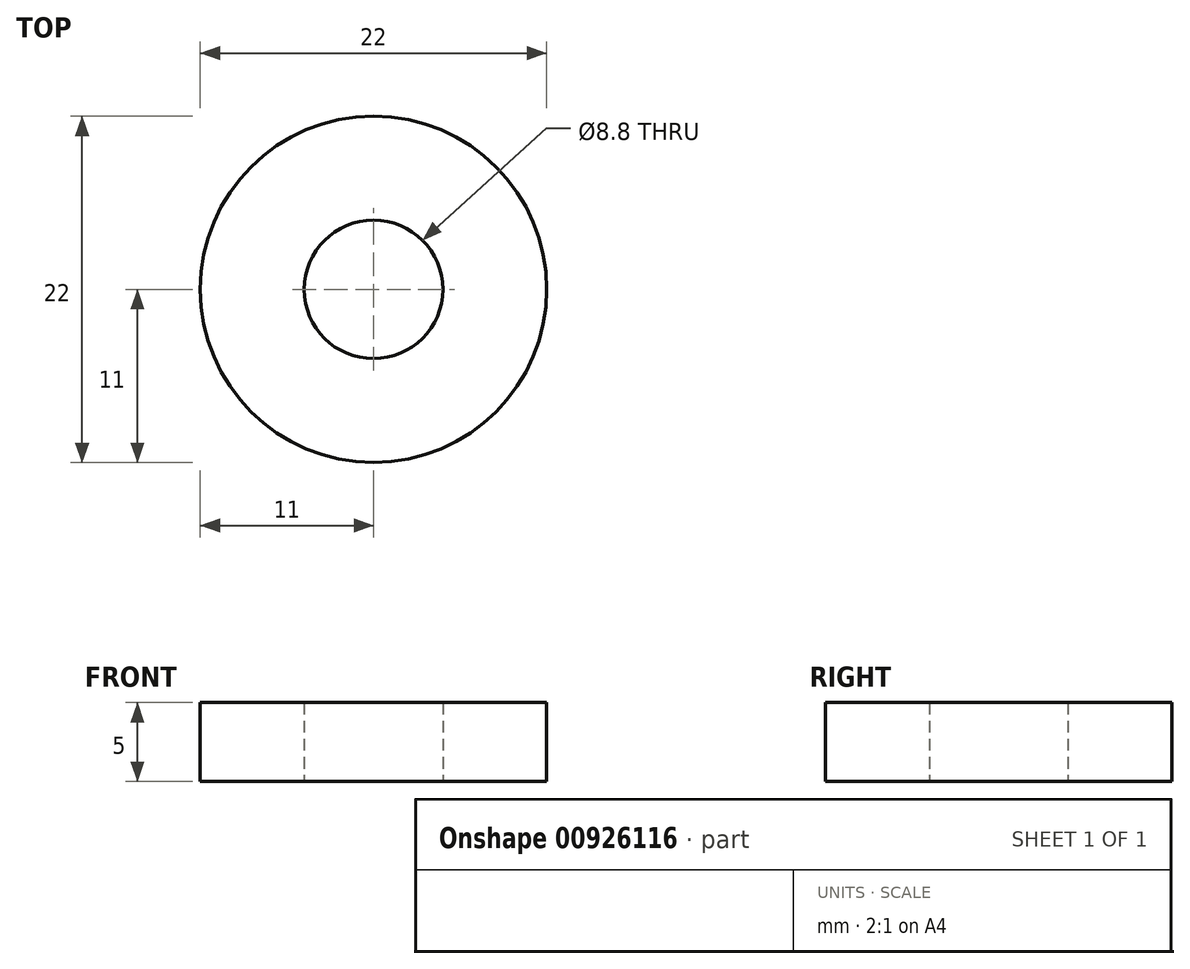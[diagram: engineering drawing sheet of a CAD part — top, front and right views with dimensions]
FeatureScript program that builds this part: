
annotation { "Feature Type Name" : "Feature", "Feature Type Description" : "" }
export const myFeature = defineFeature(function(context is Context, id is Id, definition is map)
    precondition{}
    {
        {
            var Q0;
            Q0=qCreatedBy(makeId("Top.planeOp"),FACE);
            var sketch = newSketch(context, id + "F0", { "sketchPlane" : qUnion([Q0])});
            skCircle(sketch, "E0", {"center": v(0, 0) * mm, "radius": 11 * mm});
            skCircle(sketch, "E1", {"center": v(0, 0) * mm, "radius": 4.4 * mm});
            skSolve(sketch);
        }
        {
            var Q0;
            Q0 = qSketchRegion(id + "F0", true);
            extrude(context, id + "F1", {"entities" : qUnion([Q0]), "depth" : 5 * mm, "offsetDistance" : 25 * mm});
        }
    });
